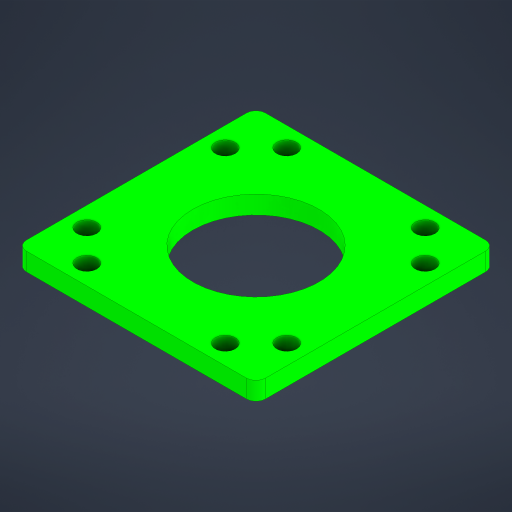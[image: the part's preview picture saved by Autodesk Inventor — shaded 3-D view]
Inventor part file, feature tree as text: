
AUTODESK INVENTOR PART (.ipt)
format: ipt  version: 2023.4 (Build 274418000, 418)  size: 214,528 bytes
history: native  units: mm
features: other x3, extrude x1, reference x1
ambient origin geometry x8: Origin, YZ Plane, XZ Plane, XY Plane, X Axis, Y Axis, Z Axis, Center Point
bodies: Solid1 (feature_tree)
feature tree (5):
  extrude  "Extrusion1"  Depth=3.75mm TaperAngle=0.0deg
  reference  "Reference1"
  parser-record x1  (decoder bookkeeping rows leaked as tree rows — omitted from the tree; the rows remain in map.json)
  other  "Cube 1x1 V5.iam"
  other  "Cube 1x1 Top V5:1"
note: 1 file-system path scrubbed to <path> (originals preserved in map.json)
